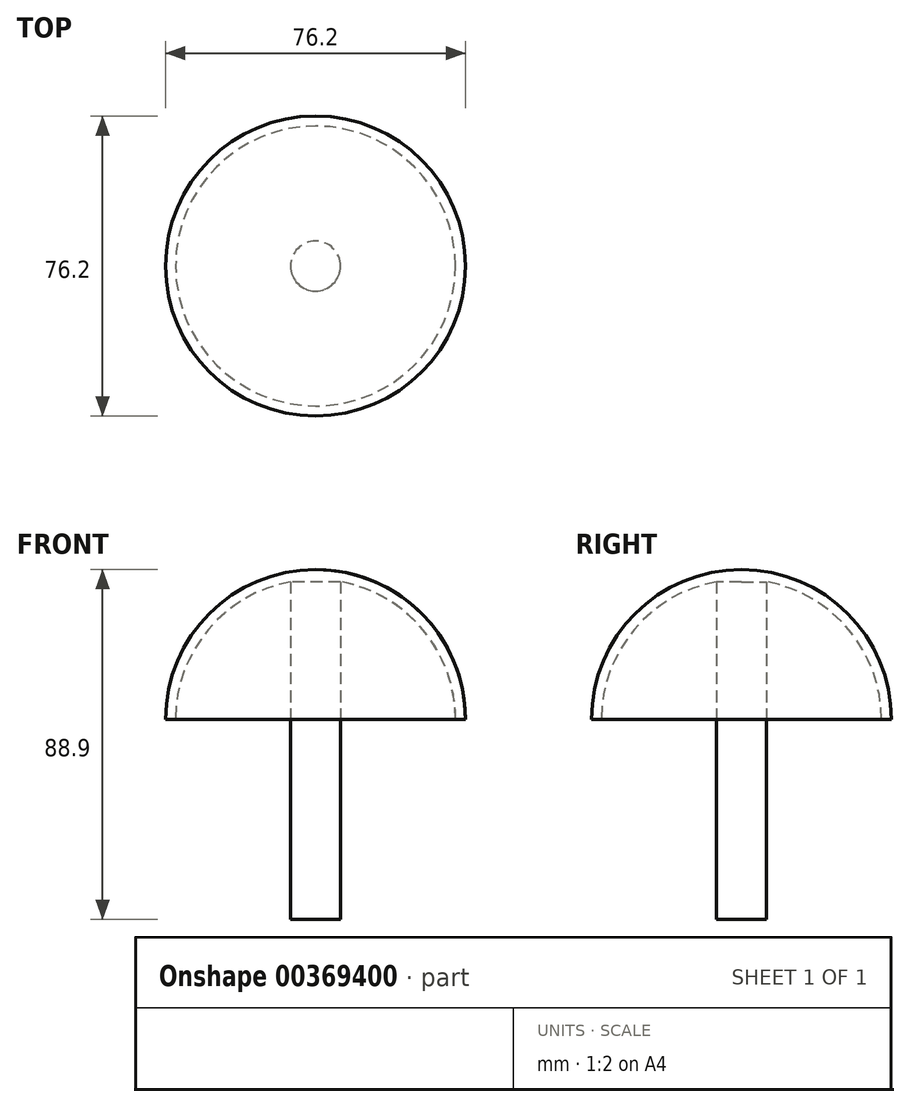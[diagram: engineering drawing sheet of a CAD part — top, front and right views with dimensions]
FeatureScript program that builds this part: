
annotation { "Feature Type Name" : "Feature", "Feature Type Description" : "" }
export const myFeature = defineFeature(function(context is Context, id is Id, definition is map)
    precondition{}
    {
        {
            var Q0;
            Q0=qCreatedBy(makeId("Top.planeOp"),FACE);
            var sketch = newSketch(context, id + "F0", { "sketchPlane" : qUnion([Q0])});
            skCircle(sketch, "E0", {"center": v(0, 0) * mm, "radius": 38.1 * mm});
            skSolve(sketch);
        }
        {
            var Q0;
            Q0=makeQuery(id+"F0.imprint","IMPRINT",FACE,{"disambiguationData":[TD([[makeQuery(id+"F0.imprint","IMPRINT",EDGE,{"derivedFrom":sQuery(id+"F0.wireOp",EDGE,"E0")}),1.0]])]});
            extrude(context, id + "F1", {"entities" : qUnion([Q0]), "depth" : 38.1 * mm});
        }
        {
            var Q0;
            Q0=makeQuery(id+"F1.opExtrude","CAP_FACE",FACE,{"disambiguationData":[OSD([sQuery(id+"F0.wireOp",EDGE,"E0")])],"isStart":false});
            fillet(context, id + "F2", {"entities" : qUnion([Q0]), "radius" : 38.1 * mm, "tangentPropagation" : true, "allowEdgeOverflow" : false});
        }
        {
            var Q0;
            Q0=makeQuery(id+"F1.opExtrude","CAP_FACE",FACE,{"disambiguationData":[OSD([sQuery(id+"F0.wireOp",EDGE,"E0")])],"isStart":true});
            shell(context, id + "F3", {"entities" : qUnion([Q0]), "thickness" : 2.54 * mm});
        }
        {
            var Q0;
            Q0=qCreatedBy(makeId("Top.planeOp"),FACE);
            var sketch = newSketch(context, id + "F4", { "sketchPlane" : qUnion([Q0])});
            skCircle(sketch, "E1", {"center": v(0, 0) * mm, "radius": 6.35 * mm});
            skSolve(sketch);
        }
        {
            var Q0;
            Q0=qSketchRegion(id+"F4",true);
            extrude(context, id + "F5", {"entities" : qUnion([Q0]), "operationType" : NewBodyOperationType.ADD, "depth" : 35.56 * mm});
        }
        {
            var Q0;
            Q0=makeQuery(id+"F4.imprint","IMPRINT",FACE,{"disambiguationData":[TD([[makeQuery(id+"F4.imprint","IMPRINT",EDGE,{"derivedFrom":sQuery(id+"F4.wireOp",EDGE,"E1")}),1.0]])]});
            var Q1;
            Q1=sQuery(id+"F4.wireOp",EDGE,"E1");
            extrude(context, id + "F6", {"entities" : qUnion([Q0]), "surfaceEntities" : qUnion([Q1]), "oppositeDirection" : true, "depth" : 50.8 * mm});
        }
    });
